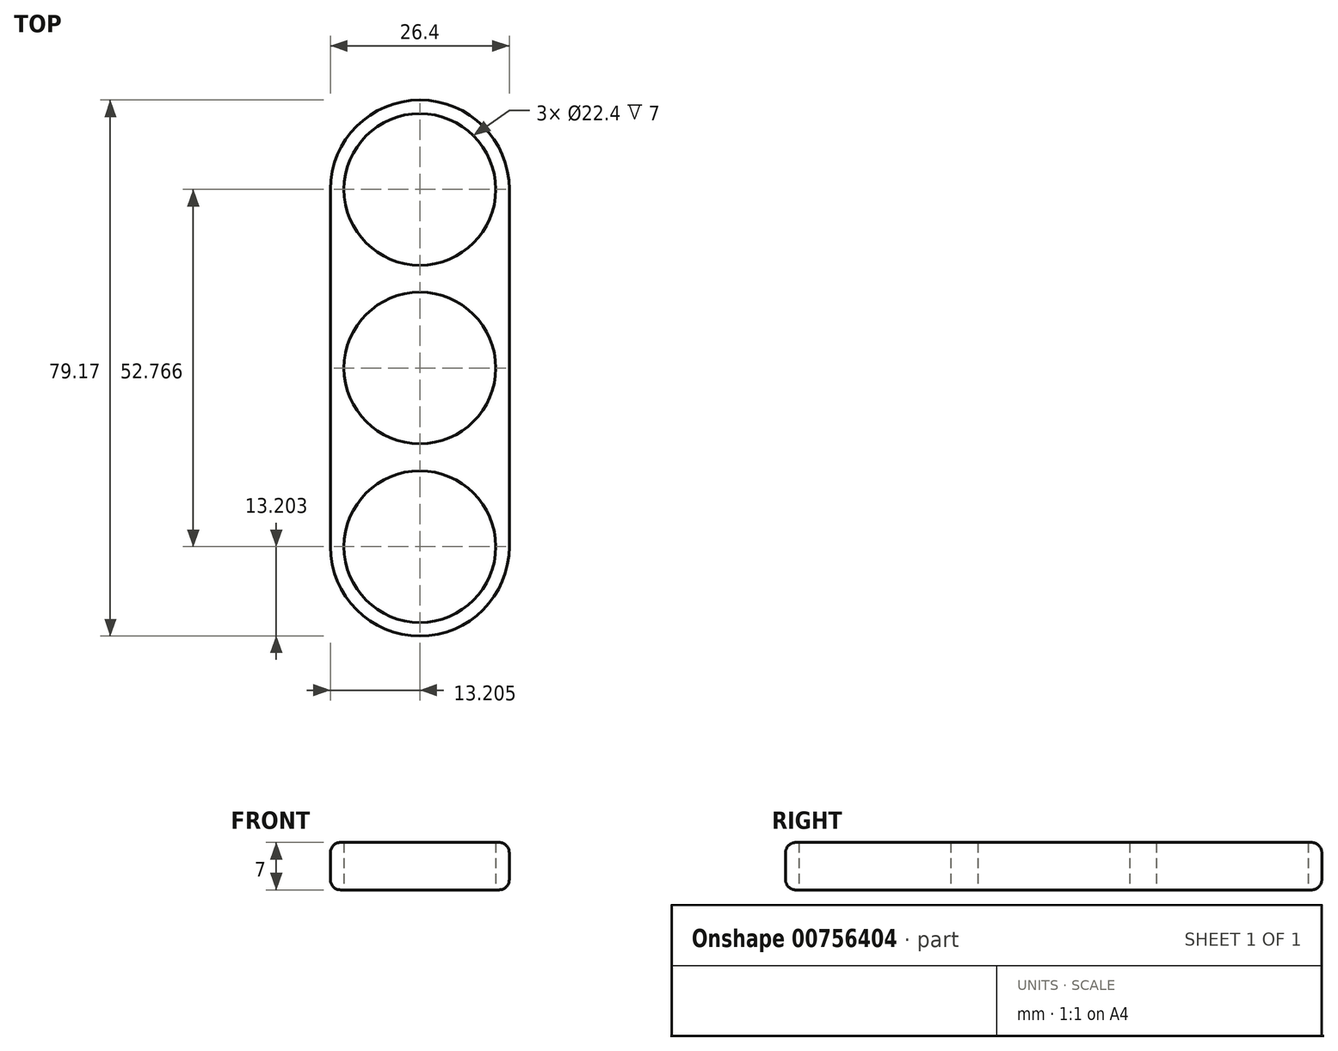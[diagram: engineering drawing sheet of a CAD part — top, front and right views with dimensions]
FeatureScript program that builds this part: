
annotation { "Feature Type Name" : "Feature", "Feature Type Description" : "" }
export const myFeature = defineFeature(function(context is Context, id is Id, definition is map)
    precondition{}
    {
        {
            var Q0;
            Q0=qCreatedBy(makeId("Top.planeOp"),FACE);
            var sketch = newSketch(context, id + "F0", { "sketchPlane" : qUnion([Q0])});
            skCircle(sketch, "E0", {"center": v(0, -0.07) * mm, "radius": 11.2 * mm});
            skCircle(sketch, "E1", {"center": v(0, 26.3) * mm, "radius": 11.2 * mm});
            skCircle(sketch, "E2.1.0", {"center": v(0, -26.46) * mm, "radius": 11.2 * mm});
            skArc(sketch, "E2.1.1", {"start": v(-13.2, -26.46) * mm, "mid": v(0, -39.66) * mm, "end": v(13.2, -26.46) * mm});
            skLineSegment(sketch, "E3", {"start": v(13.2, 26.3) * mm, "end": v(13.2, -26.46) * mm});
            skLineSegment(sketch, "E4", {"start": v(-13.2, 26.3) * mm, "end": v(-13.2, -26.46) * mm});
            skArc(sketch, "E5.trimOffspring", {"start": v(13.2, 26.3) * mm, "mid": v(0, 39.5) * mm, "end": v(-13.2, 26.3) * mm});
            skPoint(sketch, "E6.orphan", {"position": v(-25.84, 26.3) * mm});
            skPoint(sketch, "E7.orphan", {"position": v(-26.42, -26.46) * mm});
            skSolve(sketch);
        }
        {
            var Q0;
            Q0 = qSketchRegion(id + "F0", true);
            extrude(context, id + "F1", {"entities" : qUnion([Q0]), "depth" : 7 * mm, "offsetDistance" : 25 * mm});
        }
        {
            var Q0;
            Q0=makeQuery(id+"F1.opExtrude","CAP_EDGE",EDGE,{"disambiguationData":[OSD([sQuery(id+"F0.wireOp",EDGE,"E4")])],"isStart":false});
            var Q1;
            Q1=makeQuery(id+"F1.opExtrude","CAP_EDGE",EDGE,{"disambiguationData":[OSD([sQuery(id+"F0.wireOp",EDGE,"E5.trimOffspring")])],"isStart":false});
            var Q2;
            Q2=makeQuery(id+"F1.opExtrude","CAP_EDGE",EDGE,{"disambiguationData":[OSD([sQuery(id+"F0.wireOp",EDGE,"E3")])],"isStart":false});
            var Q3;
            Q3=makeQuery(id+"F1.opExtrude","CAP_EDGE",EDGE,{"disambiguationData":[OSD([sQuery(id+"F0.wireOp",EDGE,"E2.1.1")])],"isStart":false});
            fillet(context, id + "F2", {"entities" : qUnion([Q0, Q1, Q2, Q3]), "radius" : 1.5 * mm, "tangentPropagation" : true, "allowEdgeOverflow" : false});
        }
        {
            var Q0;
            Q0=makeQuery(id+"F1.opExtrude","CAP_EDGE",EDGE,{"disambiguationData":[OSD([sQuery(id+"F0.wireOp",EDGE,"E3")])],"isStart":true});
            var Q1;
            Q1=makeQuery(id+"F1.opExtrude","CAP_EDGE",EDGE,{"disambiguationData":[OSD([sQuery(id+"F0.wireOp",EDGE,"E5.trimOffspring")])],"isStart":true});
            var Q2;
            Q2=makeQuery(id+"F1.opExtrude","CAP_EDGE",EDGE,{"disambiguationData":[OSD([sQuery(id+"F0.wireOp",EDGE,"E4")])],"isStart":true});
            var Q3;
            Q3=makeQuery(id+"F1.opExtrude","CAP_EDGE",EDGE,{"disambiguationData":[OSD([sQuery(id+"F0.wireOp",EDGE,"E2.1.1")])],"isStart":true});
            fillet(context, id + "F3", {"entities" : qUnion([Q0, Q1, Q2, Q3]), "radius" : 1.5 * mm, "tangentPropagation" : true, "allowEdgeOverflow" : false});
        }
    });
